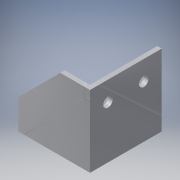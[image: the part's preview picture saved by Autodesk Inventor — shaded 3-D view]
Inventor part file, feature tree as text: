
AUTODESK INVENTOR PART (.ipt)
format: ipt  version: 2016 (Build 200138000, 138)  size: 136,192 bytes
history: native  units: in
note: dims shown in document units (in); Inventor stores cm internally (conversion verified against a paired STEP export)
features: extrude x4, sketch x4
ambient origin geometry x8: Origin, YZ Plane, XZ Plane, XY Plane, X Axis, Y Axis, Z Axis, Center Point
bodies: Solid1 (feature_tree)
feature tree (8):
  extrude  "Extrusion1"  Depth=2.0in
  extrude  "Extrusion2"  TaperAngle=135.0deg  [1 undecoded]
  extrude  "Extrusion3"  Depth=0.125in
  extrude  "Extrusion5"  Depth=0.125in
  sketch  "Sketch1"  dims[d0=2.0in d2=2.0in]
  sketch  "Sketch2"  dims[d3=2.0in d4=135.0deg]
  sketch  "Sketch3"  dims[d5=0.125in d6=0.0in d7=0.125in]
  sketch  "Sketch5"  dims[d8=2.0in d9=0.0in d10=0.2656in d11=0.2656in d14=0.5in d15=1.0in d16=0.125in d17=0.0in d25=0.547in d26=0.547in d27=0.2656in d28=0.2656in d29=0.5in d30=0.5in d31=1.0in d32=1.0in d33=0.5in d34=0.125in d35=0.0in]
note: 1 required parameter value undecoded (feature->parameter linkage not recoverable at this tier; creation-order binding heuristic only, values carry confidence <= 0.55)
